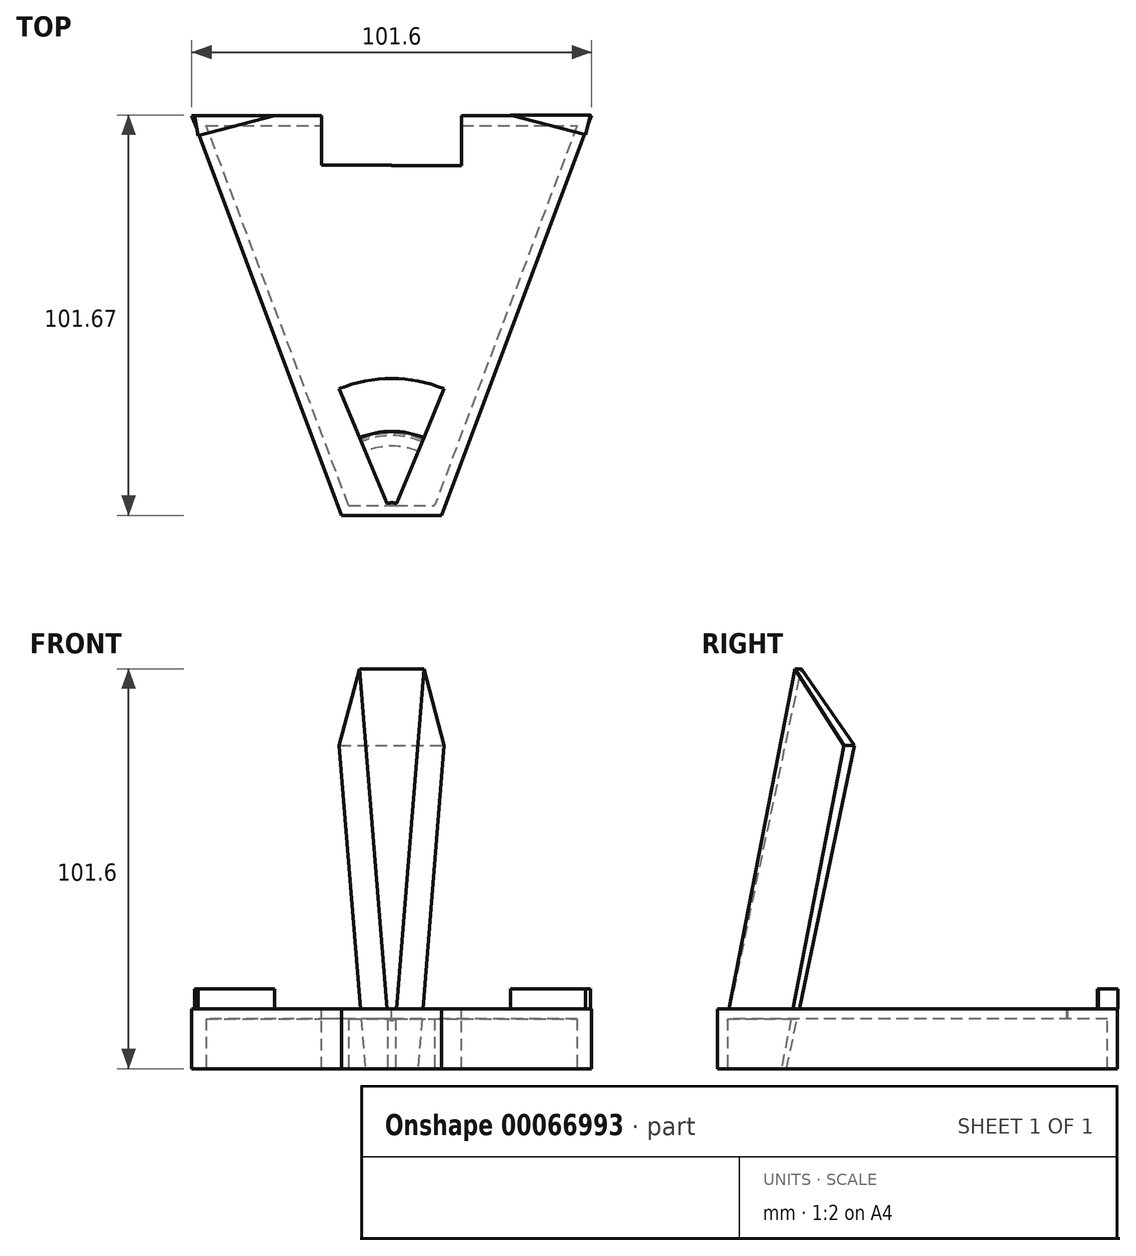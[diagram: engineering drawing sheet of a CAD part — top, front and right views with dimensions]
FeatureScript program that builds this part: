
annotation { "Feature Type Name" : "Feature", "Feature Type Description" : "" }
export const myFeature = defineFeature(function(context is Context, id is Id, definition is map)
    precondition{}
    {
        {
            var Q0;
            Q0=qCreatedBy(makeId("Top.planeOp"),FACE);
            var sketch = newSketch(context, id + "F0", { "sketchPlane" : qUnion([Q0])});
            skLineSegment(sketch, "E0", {"start": v(-12.7, 0) * mm, "end": v(-50.8, 101.6) * mm});
            skLineSegment(sketch, "E1", {"start": v(-50.8, 101.6) * mm, "end": v(50.8, 101.6) * mm});
            skLineSegment(sketch, "E2", {"start": v(50.8, 101.6) * mm, "end": v(12.7, 0) * mm});
            skLineSegment(sketch, "E3", {"start": v(-12.7, 0) * mm, "end": v(12.7, 0) * mm});
            skSolve(sketch);
        }
        {
            var Q0;
            Q0=makeQuery(id+"F0.imprint","IMPRINT",FACE,{"disambiguationData":[TD([[makeQuery(id+"F0.imprint","IMPRINT",EDGE,{"derivedFrom":sQuery(id+"F0.wireOp",EDGE,"E0")}),-1.0]])]});
            extrude(context, id + "F1", {"entities" : qUnion([Q0]), "depth" : 15.24 * mm});
        }
        {
            var Q0;
            Q0=qCreatedBy(makeId("Right.planeOp"),FACE);
            var Q1;
            Q1=qCreatedBy(makeId("Origin.pointOp"),VERTEX);
            cPlane(context, id + "F2", {"entities" : qUnion([Q0, Q1]), "cplaneType" : CPlaneType.PLANE_POINT, "offset" : 152.4 * mm, "width" : 152.4 * mm, "height" : 152.4 * mm});
        }
        {
            var Q0;
            Q0=makeQuery(id+"F1.opExtrude","CAP_FACE",FACE,{"disambiguationData":[OSD([sQuery(id+"F0.wireOp",EDGE,"E0"),sQuery(id+"F0.wireOp",EDGE,"E1"),sQuery(id+"F0.wireOp",EDGE,"E2"),sQuery(id+"F0.wireOp",EDGE,"E3")])],"isStart":true});
            shell(context, id + "F3", {"entities" : qUnion([Q0]), "thickness" : 2.54 * mm});
        }
        {
            var Q0;
            Q0=qCreatedBy(id+"F2.planeOp",FACE);
            var sketch = newSketch(context, id + "F4", { "sketchPlane" : qUnion([Q0])});
            skLineSegment(sketch, "E4", {"start": v(0, 0) * mm, "end": v(0, 101.6) * mm, "construction": true});
            skLineSegment(sketch, "E5", {"start": v(0, 0) * mm, "end": v(21.33, 101.6) * mm});
            skLineSegment(sketch, "E6", {"start": v(21.33, 101.6) * mm, "end": v(34.79, 82.06) * mm});
            skLineSegment(sketch, "E7", {"start": v(34.79, 82.06) * mm, "end": v(17.56, 0) * mm});
            skLineSegment(sketch, "E8", {"start": v(17.56, 0) * mm, "end": v(0, 0) * mm});
            skSolve(sketch);
        }
        {
            var Q0;
            Q0=makeQuery(id+"F4.imprint","IMPRINT",FACE,{"disambiguationData":[TD([[makeQuery(id+"F4.imprint","IMPRINT",EDGE,{"derivedFrom":sQuery(id+"F4.wireOp",EDGE,"E5")}),-1.0]])]});
            var Q1;
            Q1=sQuery(id+"F4.wireOp",EDGE,"E4");
            revolve(context, id + "F5", {"operationType" : NewBodyOperationType.ADD, "entities" : qUnion([Q0]), "axis" : qUnion([Q1]), "revolveType" : RevolveType.SYMMETRIC, "angle" : 45 * degree});
        }
        {
            var Q0;
            Q0=makeQuery(id+"F1.opExtrude","CAP_FACE",FACE,{"disambiguationData":[OSD([sQuery(id+"F0.wireOp",EDGE,"E0"),sQuery(id+"F0.wireOp",EDGE,"E1"),sQuery(id+"F0.wireOp",EDGE,"E2"),sQuery(id+"F0.wireOp",EDGE,"E3")])],"isStart":false});
            var Q1;
            Q1=makeQuery(id+"F1.opExtrude","CAP_VERTEX",VERTEX,{"disambiguationData":[OSD([sQuery(id+"F0.wireOp",EDGE,"E0"),sQuery(id+"F0.wireOp",EDGE,"E1")])],"isStart":false});
            cPlane(context, id + "F6", {"entities" : qUnion([Q0, Q1]), "cplaneType" : CPlaneType.PLANE_POINT, "offset" : 152.4 * mm, "width" : 152.4 * mm, "height" : 152.4 * mm});
        }
        {
            var Q0;
            Q0=qCreatedBy(id+"F6.planeOp",FACE);
            var sketch = newSketch(context, id + "F7", { "sketchPlane" : qUnion([Q0])});
            skLineSegment(sketch, "E9", {"start": v(-50.03, 101.52) * mm, "end": v(-29.7, 101.52) * mm});
            skLineSegment(sketch, "E10", {"start": v(-29.7, 101.52) * mm, "end": v(-49.22, 96.5) * mm});
            skLineSegment(sketch, "E11", {"start": v(-49.22, 96.5) * mm, "end": v(-50.03, 101.52) * mm});
            skSolve(sketch);
        }
        {
            var Q0;
            Q0=qCreatedBy(id+"F6.planeOp",FACE);
            var sketch = newSketch(context, id + "F8", { "sketchPlane" : qUnion([Q0])});
            skLineSegment(sketch, "E12", {"start": v(50.53, 101.67) * mm, "end": v(30.2, 101.67) * mm});
            skLineSegment(sketch, "E13", {"start": v(30.2, 101.67) * mm, "end": v(49.29, 96.74) * mm});
            skLineSegment(sketch, "E14", {"start": v(49.29, 96.74) * mm, "end": v(50.53, 101.67) * mm});
            skSolve(sketch);
        }
        {
            var Q0;
            Q0=makeQuery(id+"F8.imprint","IMPRINT",FACE,{"disambiguationData":[TD([[makeQuery(id+"F8.imprint","IMPRINT",EDGE,{"derivedFrom":sQuery(id+"F8.wireOp",EDGE,"E12")}),1.0]])]});
            var Q1;
            Q1=makeQuery(id+"F7.imprint","IMPRINT",FACE,{"disambiguationData":[TD([[makeQuery(id+"F7.imprint","IMPRINT",EDGE,{"derivedFrom":sQuery(id+"F7.wireOp",EDGE,"E9")}),-1.0]])]});
            extrude(context, id + "F9", {"entities" : qUnion([Q0, Q1]), "operationType" : NewBodyOperationType.ADD, "depth" : 5.08 * mm});
        }
        {
            var Q0;
            Q0=qCreatedBy(id+"F6.planeOp",FACE);
            var sketch = newSketch(context, id + "F10", { "sketchPlane" : qUnion([Q0])});
            skLineSegment(sketch, "E15.bottom", {"start": v(0, 101.73) * mm, "end": v(-17.78, 101.73) * mm});
            skLineSegment(sketch, "E15.top", {"start": v(0, 89.03) * mm, "end": v(-17.78, 89.03) * mm});
            skLineSegment(sketch, "E15.left", {"start": v(0, 101.73) * mm, "end": v(0, 89.03) * mm});
            skLineSegment(sketch, "E15.right", {"start": v(-17.78, 101.73) * mm, "end": v(-17.78, 89.03) * mm});
            skLineSegment(sketch, "E16.bottom", {"start": v(0, 101.73) * mm, "end": v(17.78, 101.73) * mm});
            skLineSegment(sketch, "E16.top", {"start": v(0, 88.8) * mm, "end": v(17.78, 88.8) * mm});
            skLineSegment(sketch, "E16.left", {"start": v(0, 101.73) * mm, "end": v(0, 88.8) * mm});
            skLineSegment(sketch, "E16.right", {"start": v(17.78, 101.73) * mm, "end": v(17.78, 88.8) * mm});
            skSolve(sketch);
        }
        {
            var Q0;
            {var subQ3=sQuery(id+"F10.wireOp",EDGE,"E16.bottom");Q0=makeQuery(id+"F10.imprint","IMPRINT",FACE,{"disambiguationData":[TD([[makeQuery(id+"F10.imprint","IMPRINT",EDGE,{"derivedFrom":subQ3}),-1.0]])]});}
            var Q1;
            {var subQ0=sQuery(id+"F10.wireOp",EDGE,"E15.bottom");Q1=makeQuery(id+"F10.imprint","IMPRINT",FACE,{"disambiguationData":[TD([[makeQuery(id+"F10.imprint","IMPRINT",EDGE,{"derivedFrom":subQ0}),1.0]])]});}
            extrude(context, id + "F11", {"entities" : qUnion([Q0, Q1]), "operationType" : NewBodyOperationType.REMOVE, "endBound" : BoundingType.THROUGH_ALL, "oppositeDirection" : true, "depth" : 25.4 * mm});
        }
    });
